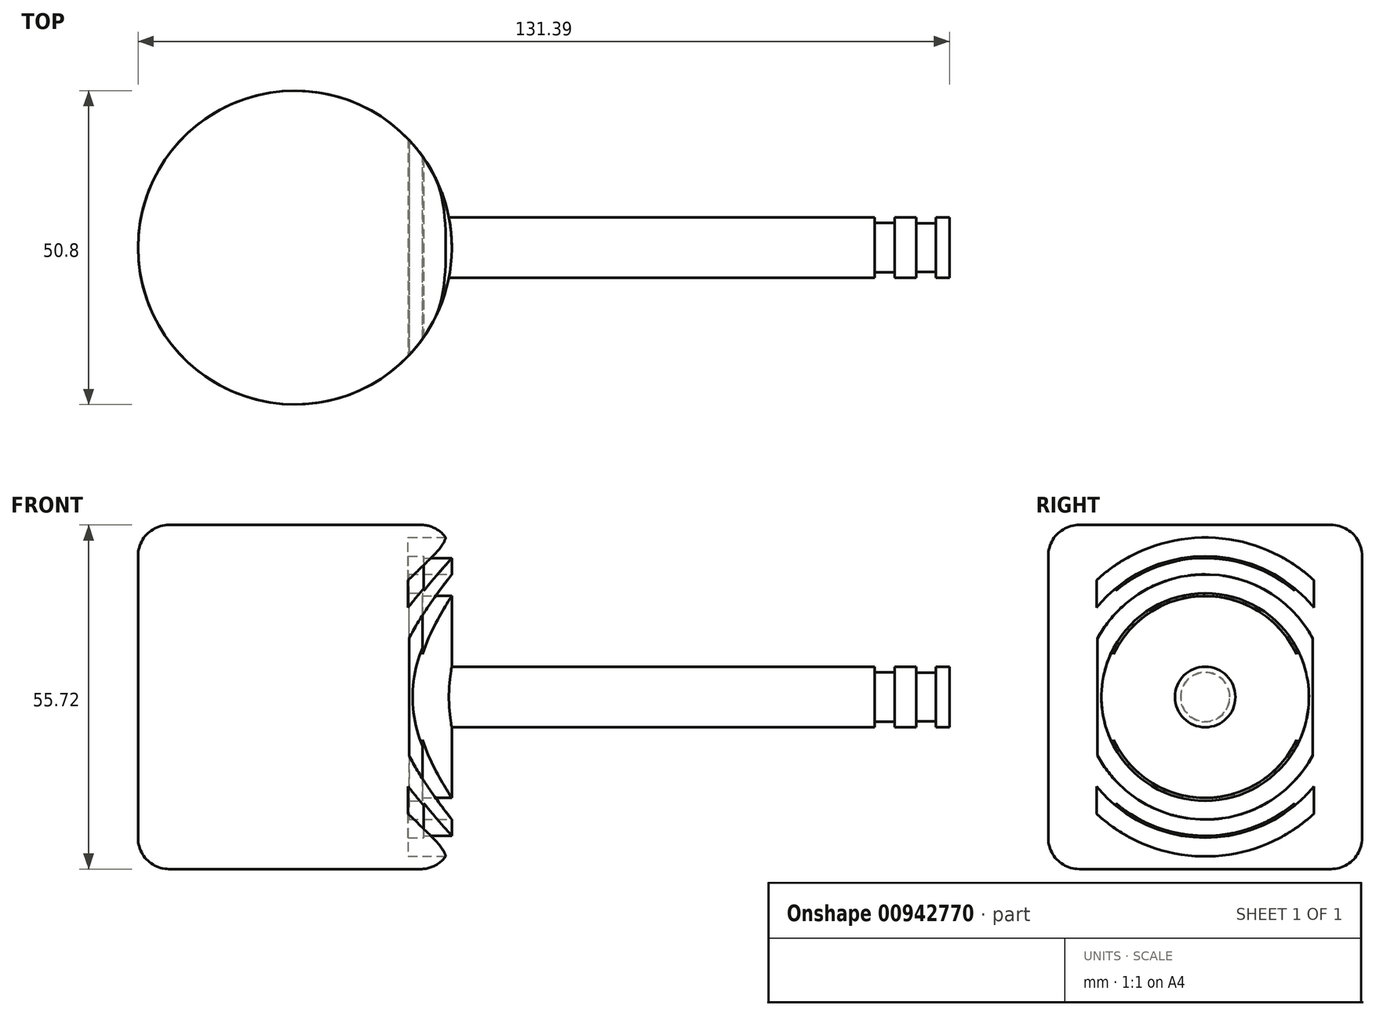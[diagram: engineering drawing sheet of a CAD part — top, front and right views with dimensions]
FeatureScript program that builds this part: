
annotation { "Feature Type Name" : "Feature", "Feature Type Description" : "" }
export const myFeature = defineFeature(function(context is Context, id is Id, definition is map)
    precondition{}
    {
        {
            var Q0;
            Q0=qCreatedBy(makeId("Front.planeOp"),FACE);
            var sketch = newSketch(context, id + "F0", { "sketchPlane" : qUnion([Q0])});
            skLineSegment(sketch, "E0.bottom", {"start": v(-12.7, 27.86) * mm, "end": v(12.7, 27.86) * mm});
            skLineSegment(sketch, "E0.top", {"start": v(-12.7, -27.86) * mm, "end": v(12.7, -27.86) * mm});
            skLineSegment(sketch, "E0.left", {"start": v(-12.7, 27.86) * mm, "end": v(-12.7, -27.86) * mm});
            skLineSegment(sketch, "E0.right", {"start": v(12.7, 27.86) * mm, "end": v(12.7, -27.86) * mm});
            skPoint(sketch, "E0.middle", {"position": v(0, 0) * mm});
            skSolve(sketch);
        }
        {
            var Q0;
            Q0 = qSketchRegion(id + "F0", true);
            var Q1;
            Q1=sQuery(id+"F0.wireOp",EDGE,"E0.right");
            revolve(context, id + "F1", {"surfaceOperationType" : NewSurfaceOperationType.NEW, "entities" : qUnion([Q0]), "axis" : qUnion([Q1]), "revolveType" : RevolveType.FULL});
        }
        {
            var Q0;
            Q0=qCreatedBy(makeId("Front.planeOp"),FACE);
            var sketch = newSketch(context, id + "F2", { "sketchPlane" : qUnion([Q0])});
            skLineSegment(sketch, "E1", {"start": v(118.7, 0) * mm, "end": v(0, 0) * mm});
            skLineSegment(sketch, "E2", {"start": v(0, 0) * mm, "end": v(0, -4.9) * mm});
            skLineSegment(sketch, "E3", {"start": v(0, -4.9) * mm, "end": v(118.7, -4.9) * mm});
            skLineSegment(sketch, "E4", {"start": v(118.7, -4.9) * mm, "end": v(118.7, 0) * mm});
            skPoint(sketch, "E5.startSnap0", {"position": v(0, -2.45) * mm});
            skSolve(sketch);
        }
        {
            var Q0;
            Q0 = qSketchRegion(id + "F2", true);
            var Q1;
            Q1=sQuery(id+"F2.wireOp",EDGE,"E1");
            revolve(context, id + "F3", {"operationType" : NewBodyOperationType.ADD, "surfaceOperationType" : NewSurfaceOperationType.NEW, "entities" : qUnion([Q0]), "axis" : qUnion([Q1]), "revolveType" : RevolveType.FULL});
        }
        {
            var Q0;
            Q0=qCreatedBy(makeId("Front.planeOp"),FACE);
            var sketch = newSketch(context, id + "F4", { "sketchPlane" : qUnion([Q0])});
            skLineSegment(sketch, "E6.bottom", {"start": v(116.48, -16.17) * mm, "end": v(113.3, -16.17) * mm});
            skLineSegment(sketch, "E6.top", {"start": v(116.48, -3.94) * mm, "end": v(113.3, -3.94) * mm});
            skLineSegment(sketch, "E6.left", {"start": v(116.48, -16.17) * mm, "end": v(116.48, -3.94) * mm});
            skLineSegment(sketch, "E6.right", {"start": v(113.3, -16.17) * mm, "end": v(113.3, -3.94) * mm});
            skPoint(sketch, "E6.middle", {"position": v(114.89, -10.06) * mm});
            skLineSegment(sketch, "E7.bottom", {"start": v(109.78, -16.25) * mm, "end": v(106.6, -16.25) * mm});
            skLineSegment(sketch, "E7.top", {"start": v(109.78, -4.02) * mm, "end": v(106.6, -4.02) * mm});
            skLineSegment(sketch, "E7.left", {"start": v(109.78, -16.25) * mm, "end": v(109.78, -4.02) * mm});
            skLineSegment(sketch, "E7.right", {"start": v(106.6, -16.25) * mm, "end": v(106.6, -4.02) * mm});
            skPoint(sketch, "E7.middle", {"position": v(108.2, -10.13) * mm});
            skLineSegment(sketch, "E8.bottom", {"start": v(54.4, -22.49) * mm, "end": v(33.57, -22.49) * mm});
            skLineSegment(sketch, "E8.top", {"start": v(54.4, -25.52) * mm, "end": v(33.57, -25.52) * mm});
            skLineSegment(sketch, "E8.left", {"start": v(54.4, -22.49) * mm, "end": v(54.4, -25.52) * mm});
            skLineSegment(sketch, "E8.right", {"start": v(33.57, -22.49) * mm, "end": v(33.57, -25.52) * mm});
            skPoint(sketch, "E8.middle", {"position": v(43.98, -24) * mm});
            skLineSegment(sketch, "E9.bottom", {"start": v(54.15, -16.35) * mm, "end": v(33.33, -16.35) * mm});
            skLineSegment(sketch, "E9.top", {"start": v(54.15, -19.38) * mm, "end": v(33.33, -19.38) * mm});
            skLineSegment(sketch, "E9.left", {"start": v(54.15, -16.35) * mm, "end": v(54.15, -19.38) * mm});
            skLineSegment(sketch, "E9.right", {"start": v(33.33, -16.35) * mm, "end": v(33.33, -19.38) * mm});
            skPoint(sketch, "E9.middle", {"position": v(43.74, -17.87) * mm});
            skLineSegment(sketch, "E10.bottom", {"start": v(51.85, 25.82) * mm, "end": v(31.03, 25.82) * mm});
            skLineSegment(sketch, "E10.top", {"start": v(51.85, 22.79) * mm, "end": v(31.03, 22.79) * mm});
            skLineSegment(sketch, "E10.left", {"start": v(51.85, 25.82) * mm, "end": v(51.85, 22.79) * mm});
            skLineSegment(sketch, "E10.right", {"start": v(31.03, 25.82) * mm, "end": v(31.03, 22.79) * mm});
            skPoint(sketch, "E10.middle", {"position": v(41.44, 24.3) * mm});
            skLineSegment(sketch, "E11.bottom", {"start": v(52, 19.84) * mm, "end": v(31.17, 19.84) * mm});
            skLineSegment(sketch, "E11.top", {"start": v(52, 16.81) * mm, "end": v(31.17, 16.81) * mm});
            skLineSegment(sketch, "E11.left", {"start": v(52, 19.84) * mm, "end": v(52, 16.81) * mm});
            skLineSegment(sketch, "E11.right", {"start": v(31.17, 19.84) * mm, "end": v(31.17, 16.81) * mm});
            skPoint(sketch, "E11.middle", {"position": v(41.58, 18.33) * mm});
            skSolve(sketch);
        }
        {
            var Q0;
            Q0=qCreatedBy(makeId("Front.planeOp"),FACE);
            var sketch = newSketch(context, id + "F5", { "sketchPlane" : qUnion([Q0])});
            skLineSegment(sketch, "E12", {"start": v(-6.16, 0) * mm, "end": v(111.34, 0) * mm, "construction": true});
            skSolve(sketch);
        }
        {
            var Q0;
            Q0=makeQuery(id+"F4.imprint","IMPRINT",FACE,{"disambiguationData":[TD([[makeQuery(id+"F4.imprint","IMPRINT",EDGE,{"derivedFrom":sQuery(id+"F4.wireOp",EDGE,"E6.bottom")}),-1.0]])]});
            var Q1;
            Q1 = qSketchRegion(id + "F5", true);
            var Q2;
            Q2=makeQuery(id+"F4.imprint","IMPRINT",FACE,{"disambiguationData":[TD([[makeQuery(id+"F4.imprint","IMPRINT",EDGE,{"derivedFrom":sQuery(id+"F4.wireOp",EDGE,"E7.bottom")}),-1.0]])]});
            var Q3;
            Q3=makeQuery(id+"F4.imprint","IMPRINT",FACE,{"disambiguationData":[TD([[makeQuery(id+"F4.imprint","IMPRINT",EDGE,{"derivedFrom":sQuery(id+"F4.wireOp",EDGE,"E8.bottom")}),1.0]])]});
            var Q4;
            Q4=makeQuery(id+"F4.imprint","IMPRINT",FACE,{"disambiguationData":[TD([[makeQuery(id+"F4.imprint","IMPRINT",EDGE,{"derivedFrom":sQuery(id+"F4.wireOp",EDGE,"E9.bottom")}),1.0]])]});
            var Q5;
            Q5=makeQuery(id+"F4.imprint","IMPRINT",FACE,{"disambiguationData":[TD([[makeQuery(id+"F4.imprint","IMPRINT",EDGE,{"derivedFrom":sQuery(id+"F4.wireOp",EDGE,"E11.bottom")}),1.0]])]});
            var Q6;
            Q6=makeQuery(id+"F4.imprint","IMPRINT",FACE,{"disambiguationData":[TD([[makeQuery(id+"F4.imprint","IMPRINT",EDGE,{"derivedFrom":sQuery(id+"F4.wireOp",EDGE,"E10.bottom")}),1.0]])]});
            var Q7;
            Q7=sQuery(id+"F5.wireOp",EDGE,"E12");
            revolve(context, id + "F6", {"operationType" : NewBodyOperationType.REMOVE, "surfaceOperationType" : NewSurfaceOperationType.NEW, "entities" : qUnion([Q0, Q1, Q2, Q3, Q4, Q5, Q6]), "axis" : qUnion([Q7]), "revolveType" : RevolveType.FULL, "oppositeDirection" : true});
        }
        {
            var Q0;
            Q0=makeQuery(id+"F1.opRevolve","SWEPT_EDGE",EDGE,{"disambiguationData":[OSD([sQuery(id+"F0.wireOp",EDGE,"E0.top"),sQuery(id+"F0.wireOp",EDGE,"E0.left")])]});
            fillet(context, id + "F7", {"entities" : qUnion([Q0]), "radius" : 5 * mm, "tangentPropagation" : true, "allowEdgeOverflow" : false});
        }
        {
            var Q0;
            Q0=makeQuery(id+"F1.opRevolve","SWEPT_EDGE",EDGE,{"disambiguationData":[OSD([sQuery(id+"F0.wireOp",EDGE,"E0.bottom"),sQuery(id+"F0.wireOp",EDGE,"E0.left")])]});
            fillet(context, id + "F8", {"entities" : qUnion([Q0]), "radius" : 5 * mm, "tangentPropagation" : true, "allowEdgeOverflow" : false});
        }
    });
